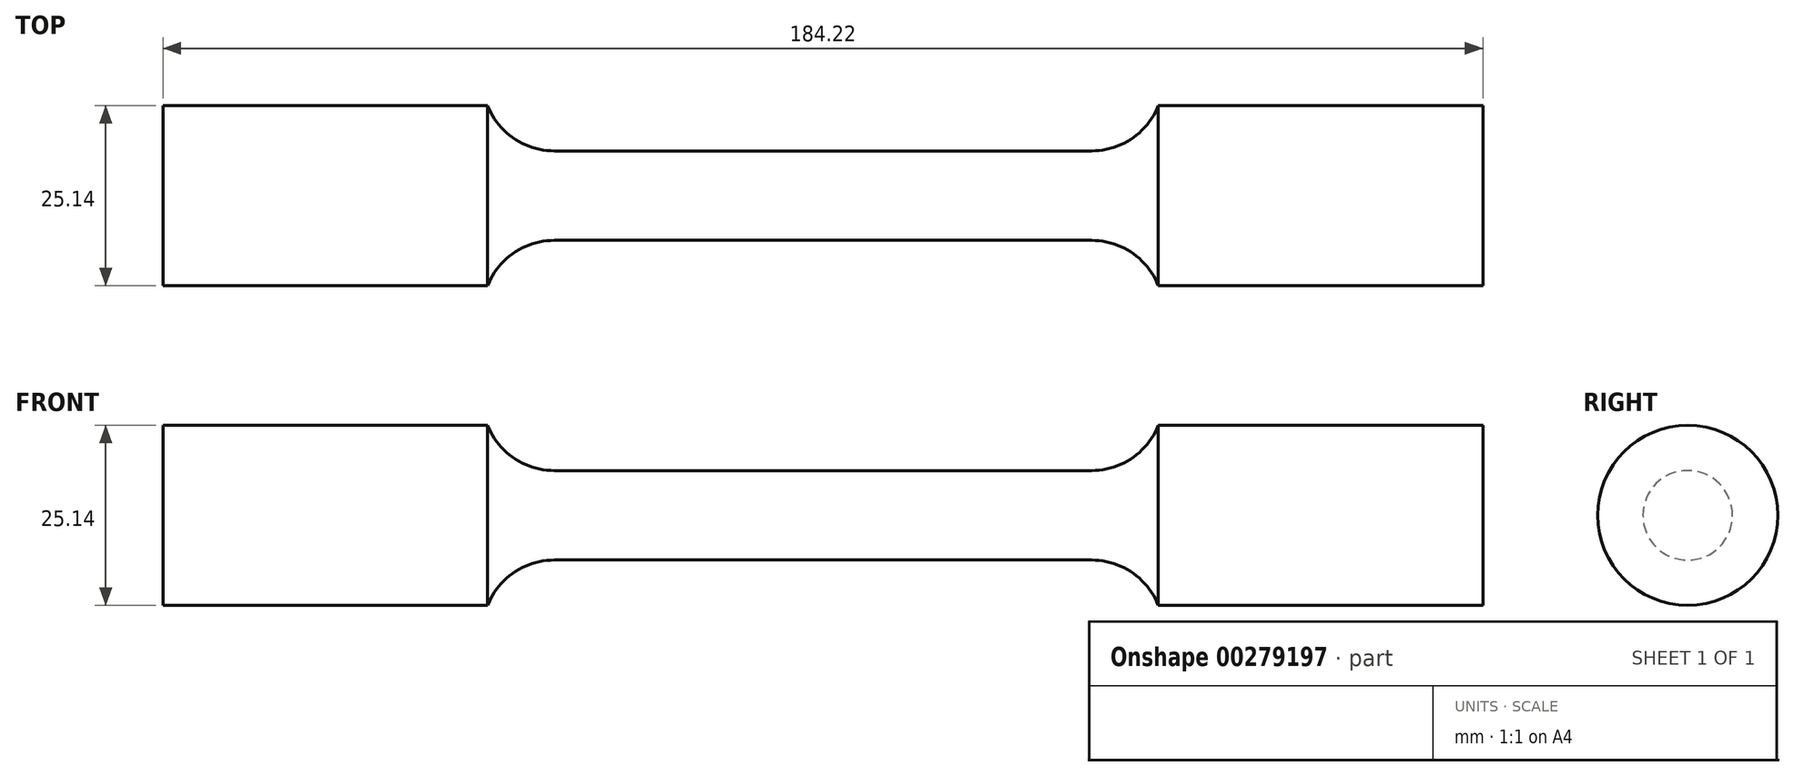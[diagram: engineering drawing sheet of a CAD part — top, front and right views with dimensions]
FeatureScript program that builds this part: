
annotation { "Feature Type Name" : "Feature", "Feature Type Description" : "" }
export const myFeature = defineFeature(function(context is Context, id is Id, definition is map)
    precondition{}
    {
        {
            var Q0;
            Q0=qCreatedBy(makeId("Front.planeOp"),FACE);
            var sketch = newSketch(context, id + "F0", { "sketchPlane" : qUnion([Q0])});
            skLineSegment(sketch, "E0", {"start": v(0, 6.25) * mm, "end": v(37.5, 6.25) * mm});
            skArc(sketch, "E1", {"start": v(37.5, 6.25) * mm, "mid": v(43.12, 7.98) * mm, "end": v(46.8, 12.57) * mm});
            skLineSegment(sketch, "E2", {"start": v(46.8, 12.57) * mm, "end": v(92.1, 12.57) * mm});
            skLineSegment(sketch, "E3", {"start": v(92.1, 0) * mm, "end": v(92.1, 12.57) * mm});
            skLineSegment(sketch, "E4.MirrorCS", {"start": v(0, 6.25) * mm, "end": v(-37.5, 6.25) * mm});
            skLineSegment(sketch, "E5.MirrorCS", {"start": v(-92.1, 0) * mm, "end": v(-92.1, 12.57) * mm});
            skLineSegment(sketch, "E6.MirrorCS", {"start": v(-46.8, 12.57) * mm, "end": v(-92.1, 12.57) * mm});
            skArc(sketch, "E7.MirrorCS", {"start": v(-37.5, 6.25) * mm, "mid": v(-43.12, 7.98) * mm, "end": v(-46.8, 12.57) * mm});
            skLineSegment(sketch, "E8", {"start": v(-92.1, 0) * mm, "end": v(92.1, 0) * mm});
            skSolve(sketch);
        }
        {
            var Q0;
            Q0=makeQuery(id+"F0.imprint","IMPRINT",FACE,{"disambiguationData":[TD([[makeQuery(id+"F0.imprint","IMPRINT",EDGE,{"derivedFrom":sQuery(id+"F0.wireOp",EDGE,"E0")}),-1.0]])]});
            var Q1;
            Q1=sQuery(id+"F0.wireOp",EDGE,"E8");
            revolve(context, id + "F1", {"entities" : qUnion([Q0]), "axis" : qUnion([Q1]), "revolveType" : RevolveType.FULL});
        }
    });
